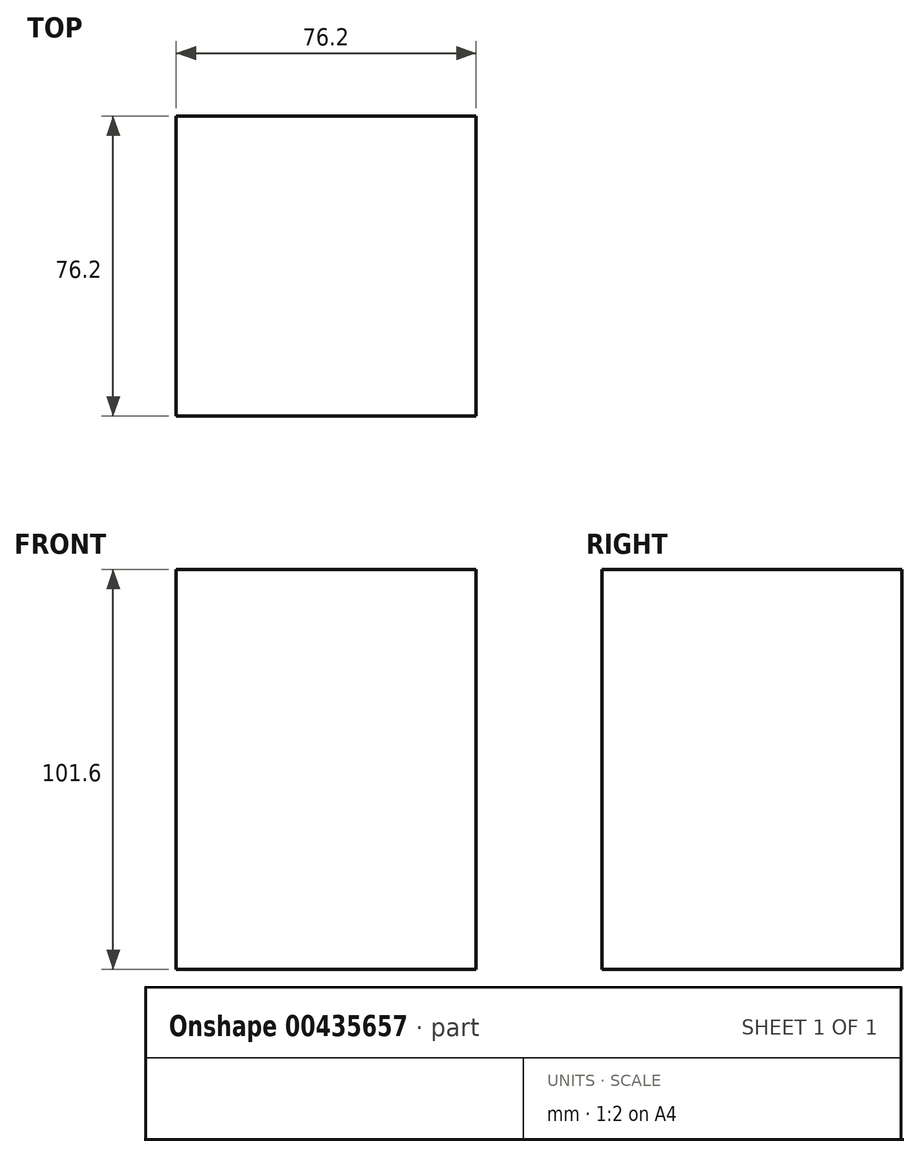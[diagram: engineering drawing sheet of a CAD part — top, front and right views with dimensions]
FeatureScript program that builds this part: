
annotation { "Feature Type Name" : "Feature", "Feature Type Description" : "" }
export const myFeature = defineFeature(function(context is Context, id is Id, definition is map)
    precondition{}
    {
        {
            var Q0;
            Q0=qCreatedBy(makeId("Top.planeOp"),FACE);
            var sketch = newSketch(context, id + "F0", { "sketchPlane" : qUnion([Q0])});
            skLineSegment(sketch, "E0.bottom", {"start": v(38.1, -38.1) * mm, "end": v(-38.1, -38.1) * mm});
            skLineSegment(sketch, "E0.top", {"start": v(38.1, 38.1) * mm, "end": v(-38.1, 38.1) * mm});
            skLineSegment(sketch, "E0.left", {"start": v(38.1, -38.1) * mm, "end": v(38.1, 38.1) * mm});
            skLineSegment(sketch, "E0.right", {"start": v(-38.1, -38.1) * mm, "end": v(-38.1, 38.1) * mm});
            skPoint(sketch, "E0.middle", {"position": v(0, 0) * mm});
            skSolve(sketch);
        }
        {
            var Q0;
            Q0=makeQuery(id+"F0.imprint","IMPRINT",FACE,{"disambiguationData":[TD([[makeQuery(id+"F0.imprint","IMPRINT",EDGE,{"derivedFrom":sQuery(id+"F0.wireOp",EDGE,"E0.bottom")}),-1.0]])]});
            extrude(context, id + "F1", {"entities" : qUnion([Q0]), "depth" : 101.6 * mm});
        }
    });
